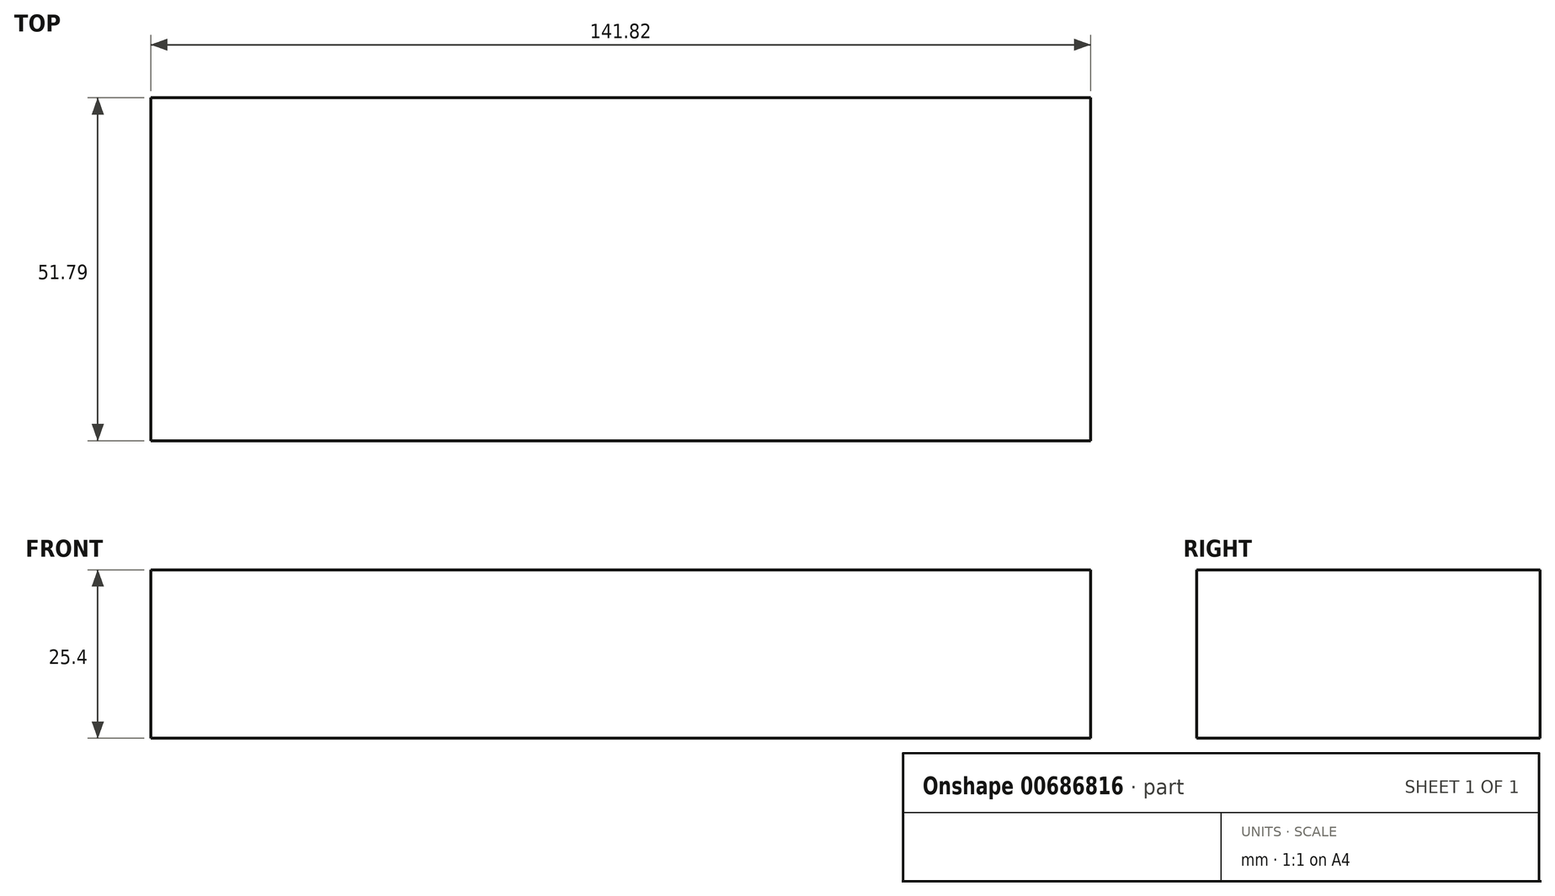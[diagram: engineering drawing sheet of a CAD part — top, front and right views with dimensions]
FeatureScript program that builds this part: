
annotation { "Feature Type Name" : "Feature", "Feature Type Description" : "" }
export const myFeature = defineFeature(function(context is Context, id is Id, definition is map)
    precondition{}
    {
        {
            var Q0;
            Q0=qCreatedBy(makeId("Top.planeOp"),FACE);
            var sketch = newSketch(context, id + "F0", { "sketchPlane" : qUnion([Q0])});
            skLineSegment(sketch, "E0.bottom", {"start": v(-70.33, 22.79) * mm, "end": v(71.49, 22.79) * mm});
            skLineSegment(sketch, "E0.top", {"start": v(-70.33, -29) * mm, "end": v(71.49, -29) * mm});
            skLineSegment(sketch, "E0.left", {"start": v(-70.33, 22.79) * mm, "end": v(-70.33, -29) * mm});
            skLineSegment(sketch, "E0.right", {"start": v(71.49, 22.79) * mm, "end": v(71.49, -29) * mm});
            skSolve(sketch);
        }
        {
            var Q0;
            Q0 = qSketchRegion(id + "F0", true);
            extrude(context, id + "F1", {"entities" : qUnion([Q0]), "depth" : 25.4 * mm, "offsetDistance" : 25.4 * mm});
        }
    });
